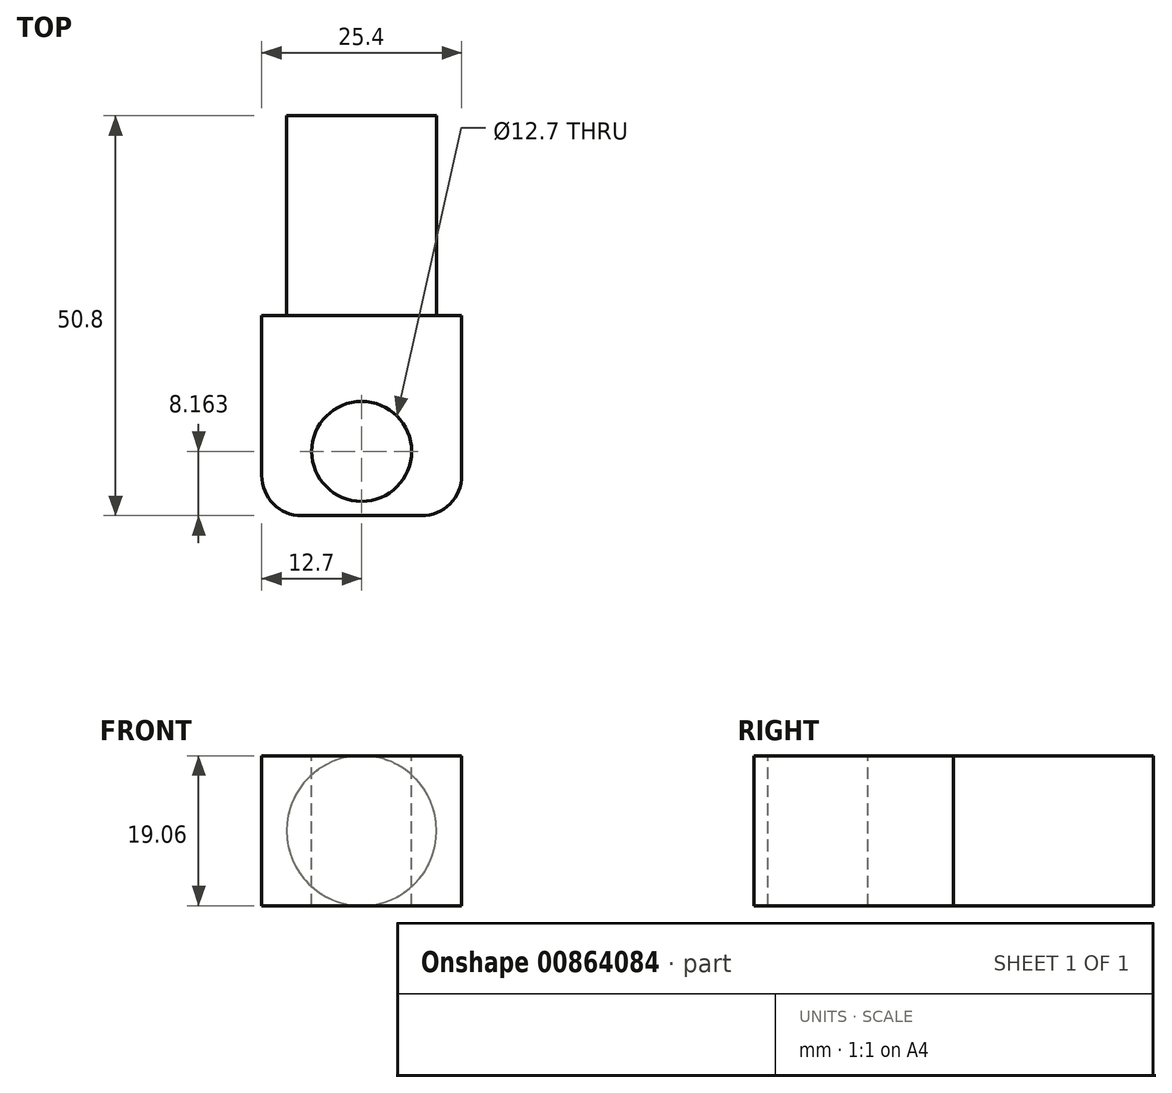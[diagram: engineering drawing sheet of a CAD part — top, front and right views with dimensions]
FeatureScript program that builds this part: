
annotation { "Feature Type Name" : "Feature", "Feature Type Description" : "" }
export const myFeature = defineFeature(function(context is Context, id is Id, definition is map)
    precondition{}
    {
        {
            var Q0;
            Q0=qCreatedBy(makeId("Front.planeOp"),FACE);
            var sketch = newSketch(context, id + "F0", { "sketchPlane" : qUnion([Q0])});
            skLineSegment(sketch, "E0.bottom", {"start": v(-12.7, -9.52) * mm, "end": v(12.7, -9.52) * mm});
            skLineSegment(sketch, "E0.top", {"start": v(-12.7, 9.53) * mm, "end": v(12.7, 9.53) * mm});
            skLineSegment(sketch, "E0.left", {"start": v(-12.7, -9.52) * mm, "end": v(-12.7, 9.53) * mm});
            skLineSegment(sketch, "E0.right", {"start": v(12.7, -9.52) * mm, "end": v(12.7, 9.53) * mm});
            skPoint(sketch, "E0.middle", {"position": v(0, 0) * mm});
            skCircle(sketch, "E1", {"center": v(0, 0) * mm, "radius": 9.53 * mm});
            skSolve(sketch);
        }
        {
            var Q0;
            {var subQ0=sQuery(id+"F0.wireOp",EDGE,"E1");var subQ1=makeQuery(id+"F0.imprint","INTERSECT",VERTEX,{"derivedFrom":[sQuery(id+"F0.wireOp",EDGE,"E0.bottom"),subQ0]});Q0=makeQuery(id+"F0.imprint","IMPRINT",FACE,{"disambiguationData":[TD([[makeQuery(id+"F0.imprint","IMPRINT",EDGE,{"disambiguationData":[TD([[subQ1,1.0]])],"derivedFrom":subQ0}),1.0]])]});}
            extrude(context, id + "F1", {"entities" : qUnion([Q0]), "oppositeDirection" : true, "depth" : 25.4 * mm, "offsetDistance" : 25.4 * mm});
        }
        {
            var Q0;
            {var subQ0=sQuery(id+"F0.wireOp",EDGE,"E0.left");Q0=makeQuery(id+"F0.imprint","IMPRINT",FACE,{"disambiguationData":[TD([[makeQuery(id+"F0.imprint","IMPRINT",EDGE,{"derivedFrom":subQ0}),-1.0]])]});}
            var Q1;
            {var subQ0=sQuery(id+"F0.wireOp",EDGE,"E0.right");Q1=makeQuery(id+"F0.imprint","IMPRINT",FACE,{"disambiguationData":[TD([[makeQuery(id+"F0.imprint","IMPRINT",EDGE,{"derivedFrom":subQ0}),1.0]])]});}
            var Q2;
            {var subQ0=sQuery(id+"F0.wireOp",EDGE,"E1");var subQ1=makeQuery(id+"F0.imprint","INTERSECT",VERTEX,{"derivedFrom":[sQuery(id+"F0.wireOp",EDGE,"E0.bottom"),subQ0]});Q2=makeQuery(id+"F0.imprint","IMPRINT",FACE,{"disambiguationData":[TD([[makeQuery(id+"F0.imprint","IMPRINT",EDGE,{"disambiguationData":[TD([[subQ1,1.0]])],"derivedFrom":subQ0}),1.0]])]});}
            extrude(context, id + "F2", {"entities" : qUnion([Q0, Q1, Q2]), "operationType" : NewBodyOperationType.ADD, "depth" : 25.4 * mm, "offsetDistance" : 25.4 * mm});
        }
        {
            var Q0;
            Q0=makeQuery(id+"F2.opExtrude","SWEPT_FACE",FACE,{"disambiguationData":[OSD([sQuery(id+"F0.wireOp",EDGE,"E0.top")])]});
            var sketch = newSketch(context, id + "F3", { "sketchPlane" : qUnion([Q0])});
            skCircle(sketch, "E2", {"center": v(0, -17.24) * mm, "radius": 6.35 * mm});
            skSolve(sketch);
        }
        {
            var Q0;
            Q0=makeQuery(id+"F3.imprint","IMPRINT",FACE,{"disambiguationData":[TD([[makeQuery(id+"F3.imprint","IMPRINT",EDGE,{"derivedFrom":sQuery(id+"F3.wireOp",EDGE,"E2")}),1.0]])]});
            extrude(context, id + "F4", {"entities" : qUnion([Q0]), "operationType" : NewBodyOperationType.REMOVE, "oppositeDirection" : true, "depth" : 25.4 * mm, "offsetDistance" : 25.4 * mm});
        }
        {
            var Q0;
            Q0=makeQuery(id+"F2.opExtrude","CAP_EDGE",EDGE,{"disambiguationData":[OSD([sQuery(id+"F0.wireOp",EDGE,"E0.left")])],"isStart":false});
            var Q1;
            Q1=makeQuery(id+"F2.opExtrude","CAP_EDGE",EDGE,{"disambiguationData":[OSD([sQuery(id+"F0.wireOp",EDGE,"E0.right")])],"isStart":false});
            fillet(context, id + "F5", {"entities" : qUnion([Q0, Q1]), "radius" : 5.08 * mm, "tangentPropagation" : true, "allowEdgeOverflow" : false});
        }
    });
